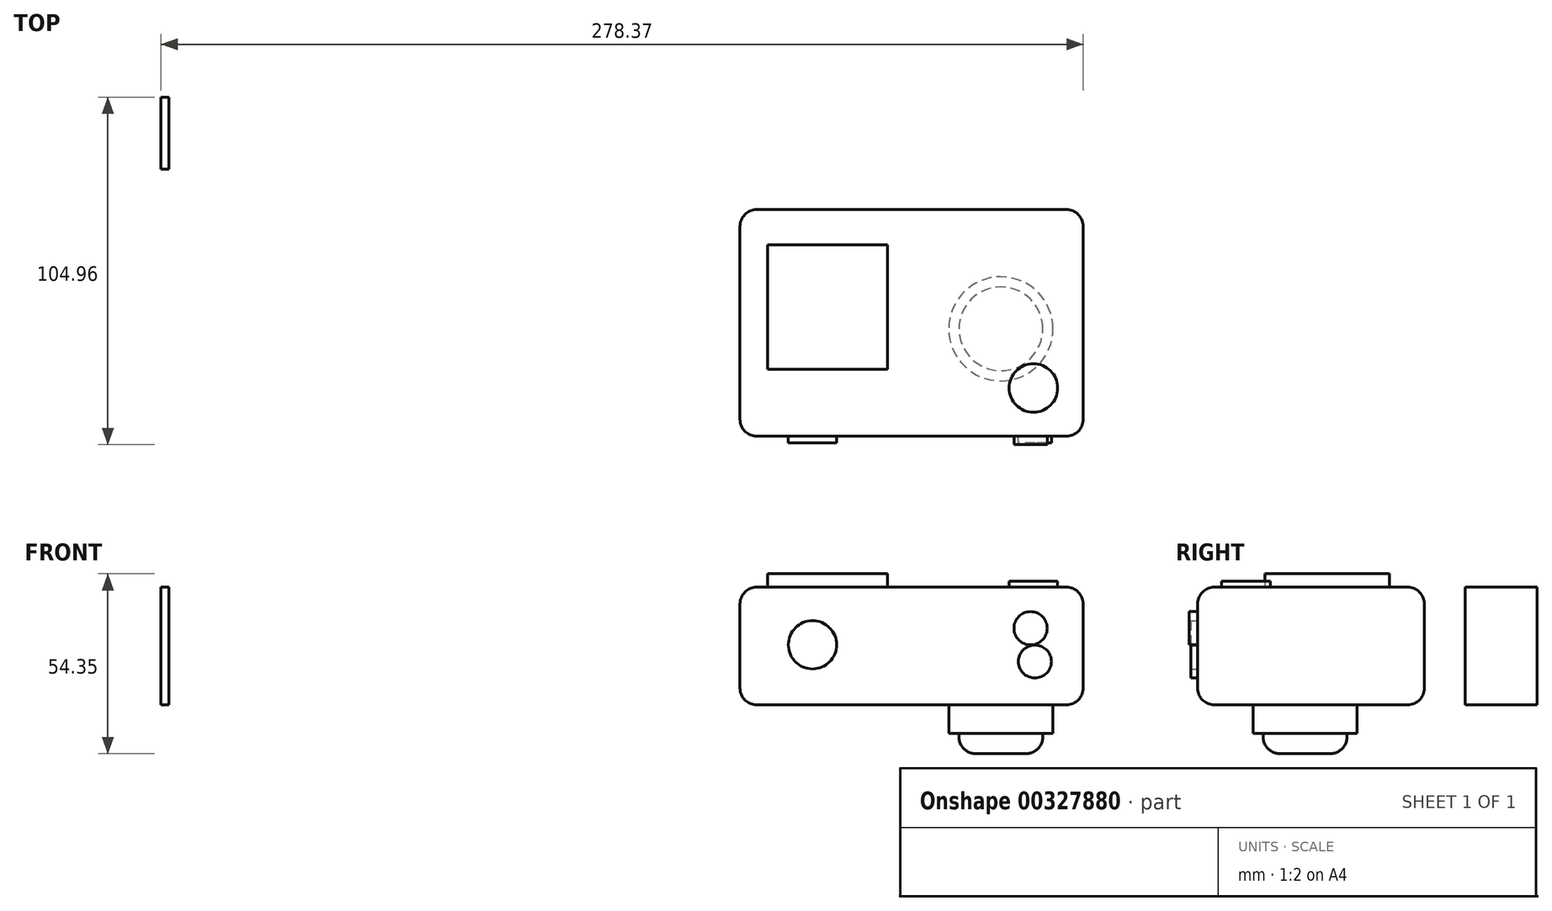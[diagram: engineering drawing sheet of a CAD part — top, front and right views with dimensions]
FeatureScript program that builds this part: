
annotation { "Feature Type Name" : "Feature", "Feature Type Description" : "" }
export const myFeature = defineFeature(function(context is Context, id is Id, definition is map)
    precondition{}
    {
        {
            var Q0;
            Q0=qCreatedBy(makeId("Top.planeOp"),FACE);
            var sketch = newSketch(context, id + "F0", { "sketchPlane" : qUnion([Q0])});
            skLineSegment(sketch, "E0.bottom", {"start": v(-61.39, 0) * mm, "end": v(42.2, 0) * mm});
            skLineSegment(sketch, "E0.top", {"start": v(-61.39, 68.45) * mm, "end": v(42.2, 68.45) * mm});
            skLineSegment(sketch, "E0.left", {"start": v(-61.39, 0) * mm, "end": v(-61.39, 68.45) * mm});
            skLineSegment(sketch, "E0.right", {"start": v(42.2, 0) * mm, "end": v(42.2, 68.45) * mm});
            skLineSegment(sketch, "E1.bottom", {"start": v(-236.16, 80.7) * mm, "end": v(-233.78, 80.7) * mm});
            skLineSegment(sketch, "E1.top", {"start": v(-236.16, 102.42) * mm, "end": v(-233.78, 102.42) * mm});
            skLineSegment(sketch, "E1.left", {"start": v(-236.16, 80.7) * mm, "end": v(-236.16, 102.42) * mm});
            skLineSegment(sketch, "E1.right", {"start": v(-233.78, 80.7) * mm, "end": v(-233.78, 102.42) * mm});
            skSolve(sketch);
        }
        {
            var Q0;
            Q0 = qSketchRegion(id + "F0", true);
            extrude(context, id + "F1", {"entities" : qUnion([Q0]), "depth" : 35.56 * mm});
        }
        {
            var Q0;
            Q0=makeQuery(id+"F1.opExtrude","CAP_EDGE",EDGE,{"disambiguationData":[OSD([sQuery(id+"F0.wireOp",EDGE,"E0.bottom")])],"isStart":false});
            var Q1;
            Q1=makeQuery(id+"F1.opExtrude","SWEPT_FACE",FACE,{"disambiguationData":[OSD([sQuery(id+"F0.wireOp",EDGE,"E0.bottom")])]});
            var Q2;
            Q2=makeQuery(id+"F1.opExtrude","SWEPT_FACE",FACE,{"disambiguationData":[OSD([sQuery(id+"F0.wireOp",EDGE,"E0.right")])]});
            var Q3;
            Q3=makeQuery(id+"F1.opExtrude","CAP_FACE",FACE,{"disambiguationData":[OSD([sQuery(id+"F0.wireOp",EDGE,"E0.bottom"),sQuery(id+"F0.wireOp",EDGE,"E0.top"),sQuery(id+"F0.wireOp",EDGE,"E0.left"),sQuery(id+"F0.wireOp",EDGE,"E0.right")])],"isStart":false});
            var Q4;
            Q4=makeQuery(id+"F1.opExtrude","CAP_EDGE",EDGE,{"disambiguationData":[OSD([sQuery(id+"F0.wireOp",EDGE,"E0.right")])],"isStart":true});
            var Q5;
            Q5=makeQuery(id+"F1.opExtrude","SWEPT_FACE",FACE,{"disambiguationData":[OSD([sQuery(id+"F0.wireOp",EDGE,"E0.left")])]});
            var Q6;
            Q6=makeQuery(id+"F1.opExtrude","CAP_FACE",FACE,{"disambiguationData":[OSD([sQuery(id+"F0.wireOp",EDGE,"E0.bottom"),sQuery(id+"F0.wireOp",EDGE,"E0.top"),sQuery(id+"F0.wireOp",EDGE,"E0.left"),sQuery(id+"F0.wireOp",EDGE,"E0.right")])],"isStart":true});
            fillet(context, id + "F2", {"entities" : qUnion([Q0, Q1, Q2, Q3, Q4, Q5, Q6]), "radius" : 5.08 * mm, "tangentPropagation" : true, "allowEdgeOverflow" : false});
        }
        {
            var Q0;
            Q0=makeQuery(id+"F1.opExtrude","CAP_FACE",FACE,{"disambiguationData":[OSD([sQuery(id+"F0.wireOp",EDGE,"E0.bottom"),sQuery(id+"F0.wireOp",EDGE,"E0.top"),sQuery(id+"F0.wireOp",EDGE,"E0.left"),sQuery(id+"F0.wireOp",EDGE,"E0.right")])],"isStart":true});
            var sketch = newSketch(context, id + "F3", { "sketchPlane" : qUnion([Q0])});
            skCircle(sketch, "E2", {"center": v(17.35, -32.44) * mm, "radius": 15.73 * mm});
            skSolve(sketch);
        }
        {
            var Q0;
            Q0 = qSketchRegion(id + "F3", true);
            extrude(context, id + "F4", {"entities" : qUnion([Q0]), "operationType" : NewBodyOperationType.ADD, "depth" : 8.64 * mm});
        }
        {
            var Q0;
            Q0=makeQuery(id+"F4.opExtrude","CAP_FACE",FACE,{"disambiguationData":[OSD([sQuery(id+"F3.wireOp",EDGE,"E2")])],"isStart":false});
            var sketch = newSketch(context, id + "F5", { "sketchPlane" : qUnion([Q0])});
            skCircle(sketch, "E3", {"center": v(17.35, -32.44) * mm, "radius": 12.65 * mm});
            skSolve(sketch);
        }
        {
            var Q0;
            Q0 = qSketchRegion(id + "F5", true);
            extrude(context, id + "F6", {"entities" : qUnion([Q0]), "operationType" : NewBodyOperationType.ADD, "depth" : 6.1 * mm});
        }
        {
            var Q0;
            Q0=makeQuery(id+"F6.opExtrude","CAP_FACE",FACE,{"disambiguationData":[OSD([sQuery(id+"F5.wireOp",EDGE,"E3")])],"isStart":false});
            fillet(context, id + "F7", {"entities" : qUnion([Q0]), "radius" : 5.08 * mm, "tangentPropagation" : true, "allowEdgeOverflow" : false});
        }
        {
            var Q0;
            Q0=makeQuery(id+"F1.opExtrude","CAP_FACE",FACE,{"disambiguationData":[OSD([sQuery(id+"F0.wireOp",EDGE,"E0.bottom"),sQuery(id+"F0.wireOp",EDGE,"E0.top"),sQuery(id+"F0.wireOp",EDGE,"E0.left"),sQuery(id+"F0.wireOp",EDGE,"E0.right")])],"isStart":false});
            var sketch = newSketch(context, id + "F8", { "sketchPlane" : qUnion([Q0])});
            skLineSegment(sketch, "E4.bottom", {"start": v(-16.81, 20.24) * mm, "end": v(-53.06, 20.24) * mm});
            skLineSegment(sketch, "E4.top", {"start": v(-16.81, 57.84) * mm, "end": v(-53.06, 57.84) * mm});
            skLineSegment(sketch, "E4.left", {"start": v(-16.81, 20.24) * mm, "end": v(-16.81, 57.84) * mm});
            skLineSegment(sketch, "E4.right", {"start": v(-53.06, 20.24) * mm, "end": v(-53.06, 57.84) * mm});
            skSolve(sketch);
        }
        {
            var Q0;
            Q0 = qSketchRegion(id + "F8", true);
            extrude(context, id + "F9", {"entities" : qUnion([Q0]), "operationType" : NewBodyOperationType.ADD, "depth" : 4.06 * mm});
        }
        {
            var Q0;
            Q0=makeQuery(id+"F1.opExtrude","SWEPT_FACE",FACE,{"disambiguationData":[OSD([sQuery(id+"F0.wireOp",EDGE,"E0.bottom")])]});
            var sketch = newSketch(context, id + "F10", { "sketchPlane" : qUnion([Q0])});
            skCircle(sketch, "E5", {"center": v(-39.5, 18.17) * mm, "radius": 7.28 * mm});
            skSolve(sketch);
        }
        {
            var Q0;
            Q0 = qSketchRegion(id + "F10", true);
            extrude(context, id + "F11", {"entities" : qUnion([Q0]), "operationType" : NewBodyOperationType.ADD, "depth" : 2.03 * mm});
        }
        {
            var Q0;
            Q0=makeQuery(id+"F1.opExtrude","SWEPT_FACE",FACE,{"disambiguationData":[OSD([sQuery(id+"F0.wireOp",EDGE,"E0.bottom")])]});
            var sketch = newSketch(context, id + "F12", { "sketchPlane" : qUnion([Q0])});
            skCircle(sketch, "E6", {"center": v(27.62, 13.11) * mm, "radius": 4.98 * mm});
            skSolve(sketch);
        }
        {
            var Q0;
            Q0 = qSketchRegion(id + "F12", true);
            extrude(context, id + "F13", {"entities" : qUnion([Q0]), "operationType" : NewBodyOperationType.ADD, "depth" : 2.03 * mm});
        }
        {
            var Q0;
            Q0=makeQuery(id+"F1.opExtrude","SWEPT_FACE",FACE,{"disambiguationData":[OSD([sQuery(id+"F0.wireOp",EDGE,"E0.bottom")])]});
            var sketch = newSketch(context, id + "F14", { "sketchPlane" : qUnion([Q0])});
            skCircle(sketch, "E7", {"center": v(26.32, 23.16) * mm, "radius": 5.01 * mm});
            skSolve(sketch);
        }
        {
            var Q0;
            Q0 = qSketchRegion(id + "F14", true);
            extrude(context, id + "F15", {"entities" : qUnion([Q0]), "operationType" : NewBodyOperationType.ADD, "depth" : 2.54 * mm});
        }
        {
            var Q0;
            Q0=makeQuery(id+"F1.opExtrude","CAP_FACE",FACE,{"disambiguationData":[OSD([sQuery(id+"F0.wireOp",EDGE,"E0.bottom"),sQuery(id+"F0.wireOp",EDGE,"E0.top"),sQuery(id+"F0.wireOp",EDGE,"E0.left"),sQuery(id+"F0.wireOp",EDGE,"E0.right")])],"isStart":false});
            var sketch = newSketch(context, id + "F16", { "sketchPlane" : qUnion([Q0])});
            skCircle(sketch, "E8", {"center": v(27.18, 14.58) * mm, "radius": 7.33 * mm});
            skSolve(sketch);
        }
        {
            var Q0;
            Q0 = qSketchRegion(id + "F16", true);
            extrude(context, id + "F17", {"entities" : qUnion([Q0]), "operationType" : NewBodyOperationType.ADD, "depth" : 1.78 * mm});
        }
    });
